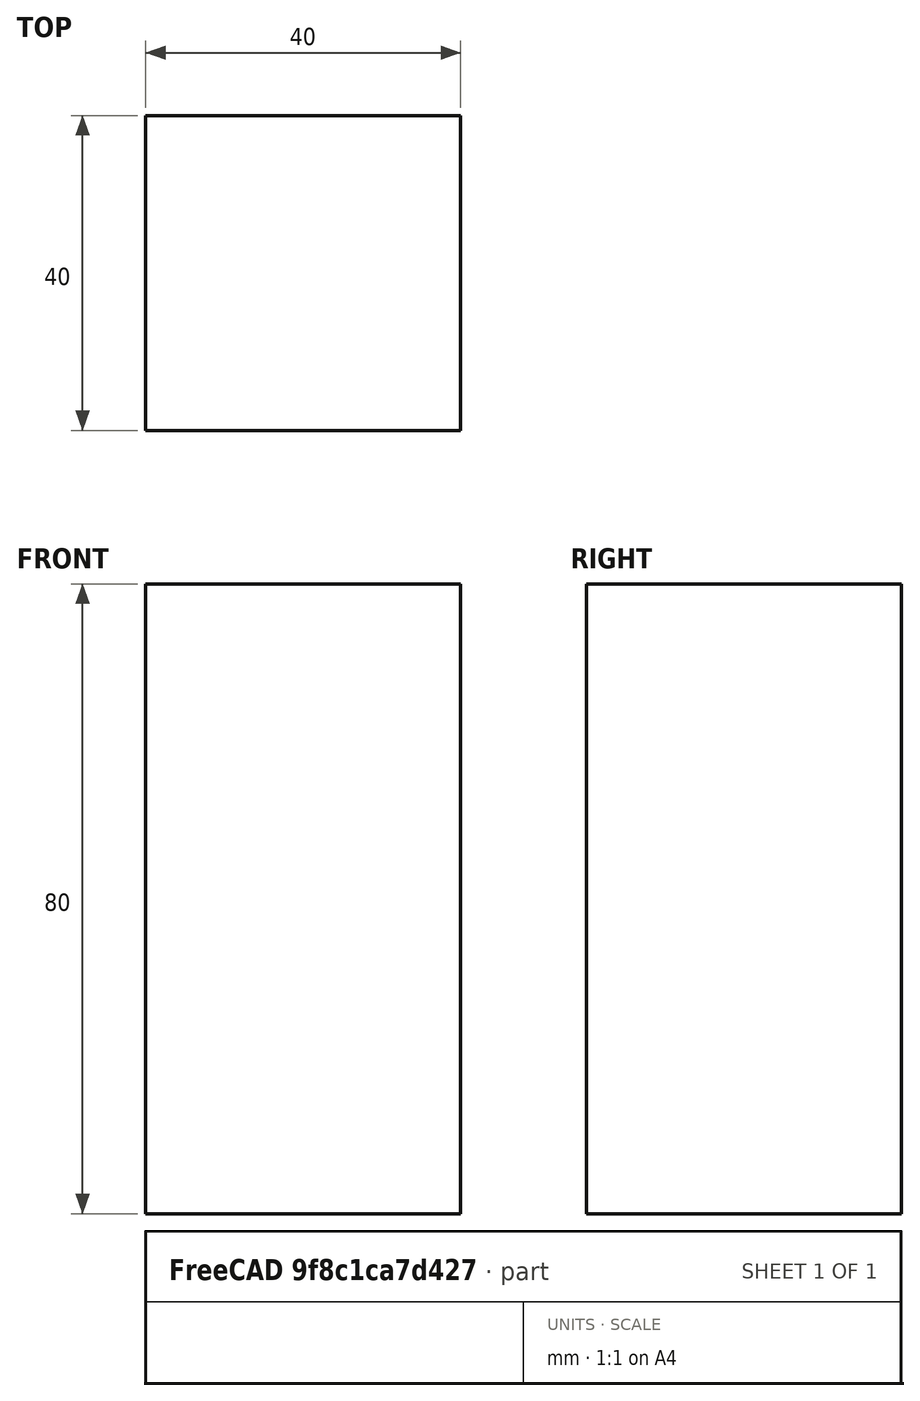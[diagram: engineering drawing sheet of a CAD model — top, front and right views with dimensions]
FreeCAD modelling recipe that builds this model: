
FCSTD DOCUMENT  (FreeCAD 0.18R16110 (Git))
Label: squartube
License: All rights reserved
LicenseURL: http://en.wikipedia.org/wiki/All_rights_reserved
objects: Sketcher::SketchObject×1, PartDesign::Pad×1, PartDesign::Body×1
note: 4 computed .brp shape members not serialized (recipe doc carries the construction recipe); baked Part::Feature solids carry a one-line shape summary decoded from their .brp

FEATURE [Sketcher::SketchObject] Sketch
  MapMode = 5
  Support = -> [XY_Plane]
  sketch-geometry (4):
    g0: LineSegment StartX=0 StartY=40 StartZ=0 EndX=40 EndY=40 EndZ=0
    g1: LineSegment StartX=40 StartY=40 StartZ=0 EndX=40 EndY=0 EndZ=0
    g2: LineSegment StartX=40 StartY=0 StartZ=0 EndX=0 EndY=0 EndZ=0
    g3: LineSegment StartX=0 StartY=0 StartZ=0 EndX=0 EndY=40 EndZ=0
  constraints (11):
    c: Coincident(g0,g1)
    c: Coincident(g1,g2)
    c: Coincident(g2,g3)
    c: Coincident(g3,g0)
    c: Horizontal(g0)
    c: Horizontal(g2)
    c: Vertical(g1)
    c: Vertical(g3)
    c: DistanceY(g3,g3) = 40
    c: DistanceX(g2,g2) = 40
    c: Coincident(g2,g-1)
FEATURE [PartDesign::Pad] Pad
  Length = 80
  Length2 = 100
  Profile = -> Sketch
  Type = 0
FEATURE [PartDesign::Body] Body
  Group = -> [Sketch,Pad]
  Origin = -> Origin
  Tip = -> Pad
